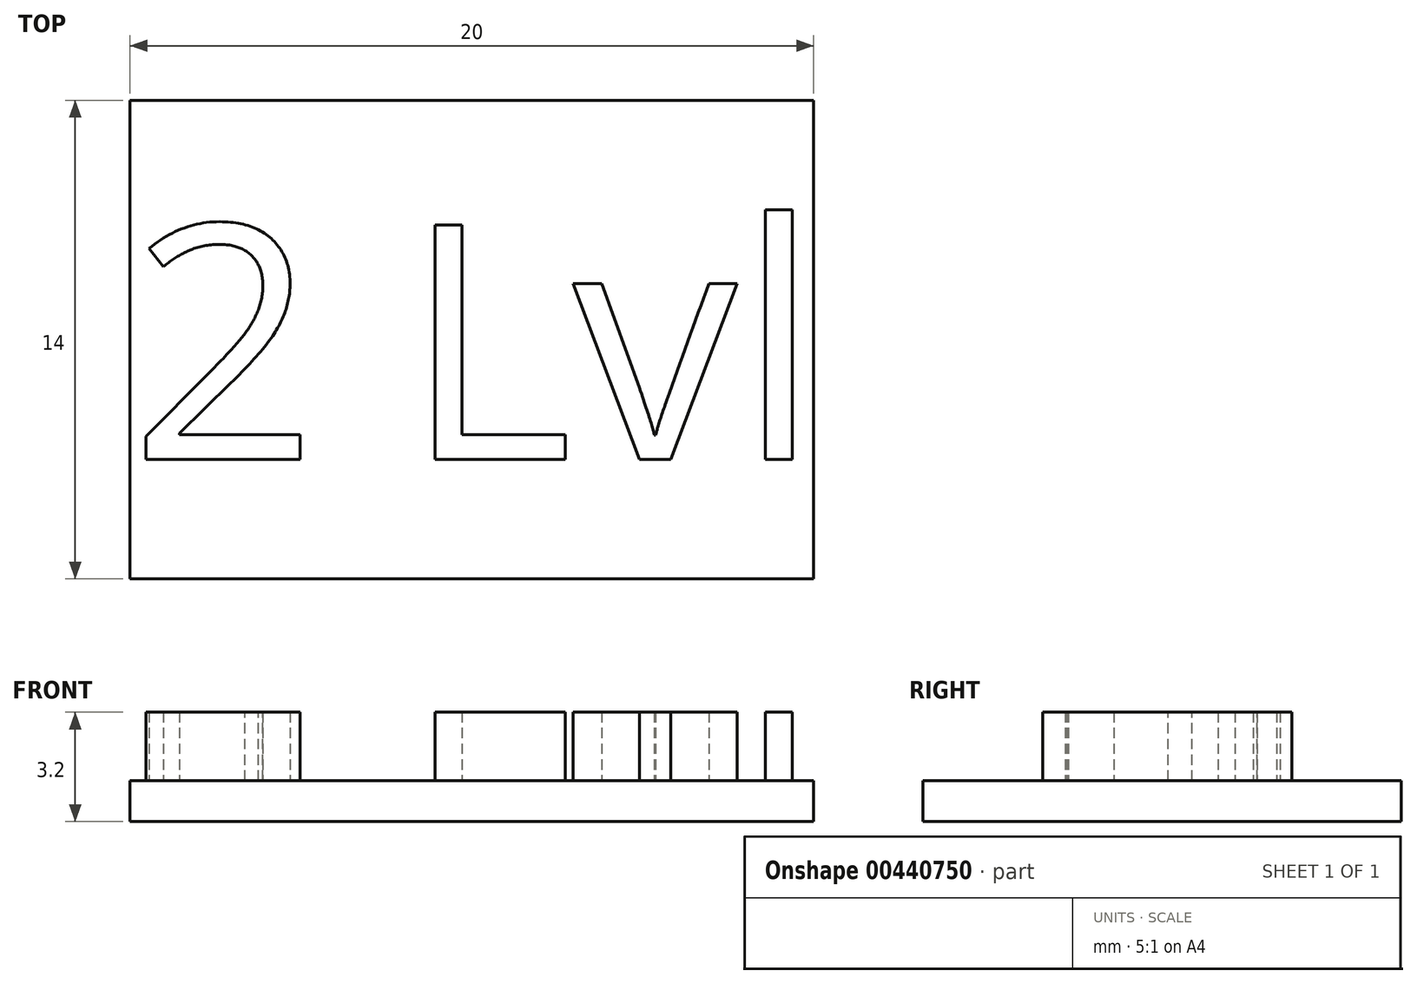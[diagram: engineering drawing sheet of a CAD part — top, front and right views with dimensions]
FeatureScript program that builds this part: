
annotation { "Feature Type Name" : "Feature", "Feature Type Description" : "" }
export const myFeature = defineFeature(function(context is Context, id is Id, definition is map)
    precondition{}
    {
        {
            var Q0;
            Q0=qCreatedBy(makeId("Top.planeOp"),FACE);
            var sketch = newSketch(context, id + "F0", { "sketchPlane" : qUnion([Q0])});
            skLineSegment(sketch, "E0.bottom", {"start": v(0, 0) * mm, "end": v(20, 0) * mm});
            skLineSegment(sketch, "E0.top", {"start": v(0, 14) * mm, "end": v(20, 14) * mm});
            skLineSegment(sketch, "E0.left", {"start": v(0, 0) * mm, "end": v(0, 14) * mm});
            skLineSegment(sketch, "E0.right", {"start": v(20, 0) * mm, "end": v(20, 14) * mm});
            skSolve(sketch);
        }
        {
            var Q0;
            Q0=qSketchRegion(id+"F0",true);
            extrude(context, id + "F1", {"entities" : qUnion([Q0]), "depth" : 1.2 * mm});
        }
        {
            var Q0;
            Q0=makeQuery(id+"F1.opExtrude","CAP_FACE",FACE,{"disambiguationData":[OSD([sQuery(id+"F0.wireOp",EDGE,"E0.bottom"),sQuery(id+"F0.wireOp",EDGE,"E0.top"),sQuery(id+"F0.wireOp",EDGE,"E0.left"),sQuery(id+"F0.wireOp",EDGE,"E0.right")])],"isStart":false});
            var sketch = newSketch(context, id + "F2", { "sketchPlane" : qUnion([Q0])});
            skText(sketch, "E1", { "text": "2 Lvl", "fontName": "OpenSans-Regular.ttf"});
            const initialGuessF2  = {"E1": [0, 0.0035, 1, 0, 0.00691]};
            skSetInitialGuess(sketch, initialGuessF2);
            skSolve(sketch);
        }
        {
            var Q0;
            Q0=qSketchRegion(id+"F2",true);
            extrude(context, id + "F3", {"entities" : qUnion([Q0]), "operationType" : NewBodyOperationType.ADD, "depth" : 2 * mm});
        }
    });
